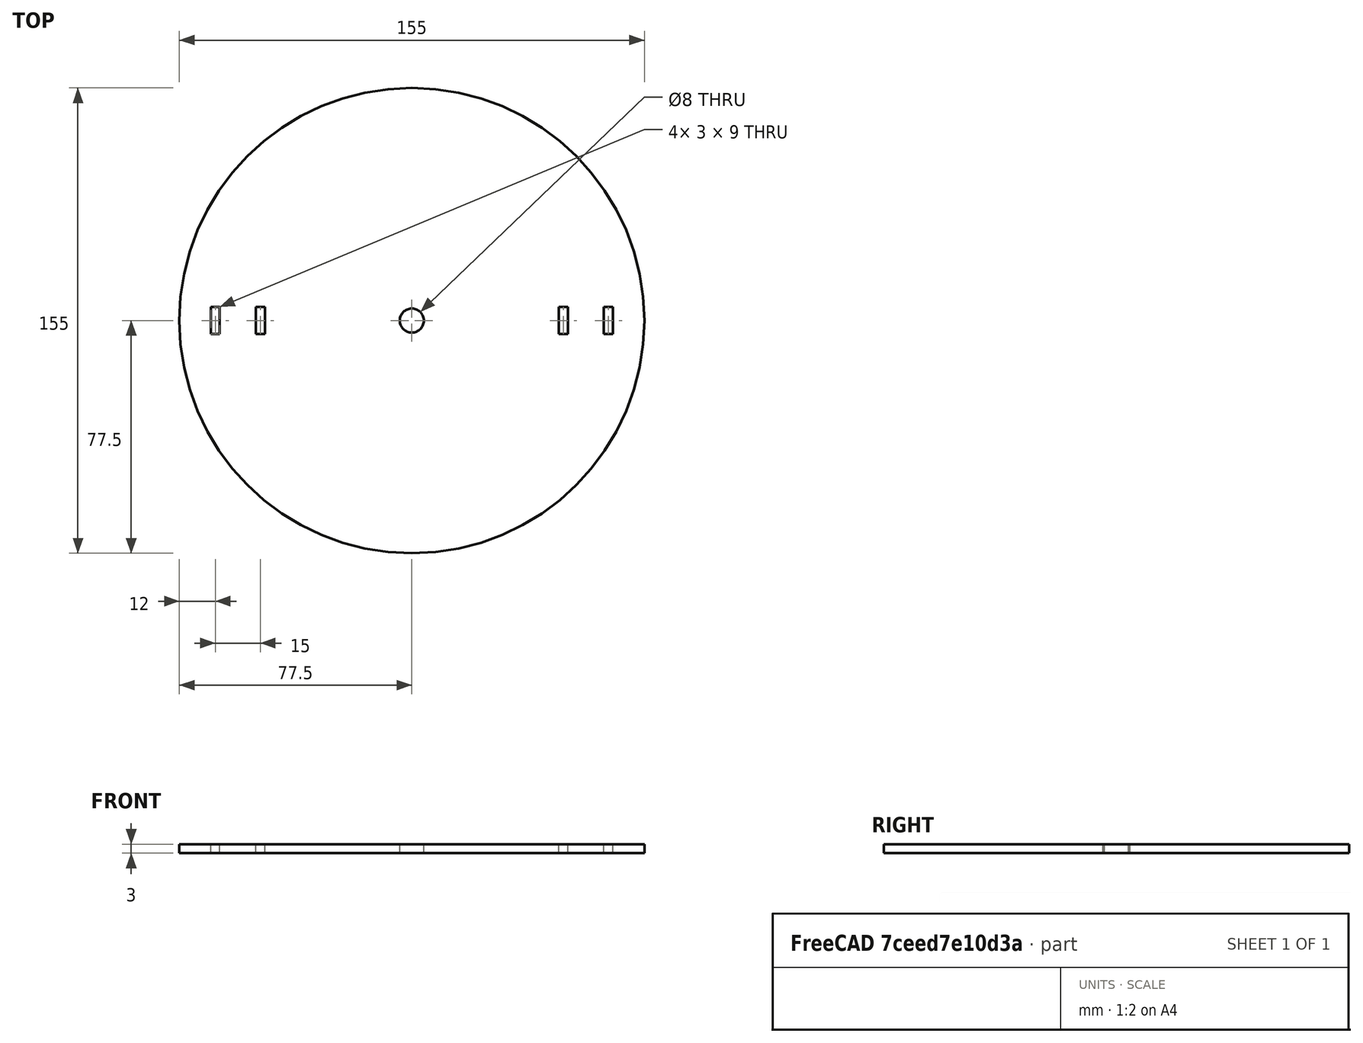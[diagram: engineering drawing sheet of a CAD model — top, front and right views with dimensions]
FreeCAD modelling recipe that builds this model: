
FCSTD DOCUMENT  (FreeCAD 0.16R6707 (Git))
Label: turretBasis
License: All rights reserved
LicenseURL: http://en.wikipedia.org/wiki/All_rights_reserved
objects: Part::Cut×5, Part::Box×4, Part::Cylinder×2
note: 11 computed .brp shape members not serialized (recipe doc carries the construction recipe); baked Part::Feature solids carry a one-line shape summary decoded from their .brp

FEATURE [Part::Cylinder] Cylinder
  Angle = 360
  Height = 3
  Radius = 77.5
FEATURE [Part::Cylinder] Cylinder017  label="Cylinder001"
  Angle = 360
  Height = 3
  Radius = 4
FEATURE [Part::Cut] Cut  label="cut002"
  Base = -> Cylinder
  Tool = -> Cylinder017
FEATURE [Part::Box] Box  label="Cube"
  Height = 3
  Length = 3
  Placement = pos=(-52,-4.5,0) rot=(0,0,1;0rad)
  Width = 9
FEATURE [Part::Box] Box126  label="Cube048"
  Height = 3
  Length = 3
  Placement = pos=(-67,-4.5,0) rot=(0,0,1;0rad)
  Width = 9
FEATURE [Part::Box] Box127  label="Cube049"
  Height = 3
  Length = 3
  Placement = pos=(49,-4.5,0) rot=(0,0,1;0rad)
  Width = 9
FEATURE [Part::Box] Box128  label="Cube050"
  Height = 3
  Length = 3
  Placement = pos=(64,-4.5,0) rot=(0,0,1;0rad)
  Width = 9
FEATURE [Part::Cut] Cut001
  Base = -> Cut
  Tool = -> Box126
FEATURE [Part::Cut] Cut002
  Base = -> Cut001
  Tool = -> Box
FEATURE [Part::Cut] Cut003
  Base = -> Cut002
  Tool = -> Box128
FEATURE [Part::Cut] Cut004
  Base = -> Cut003
  Tool = -> Box127
